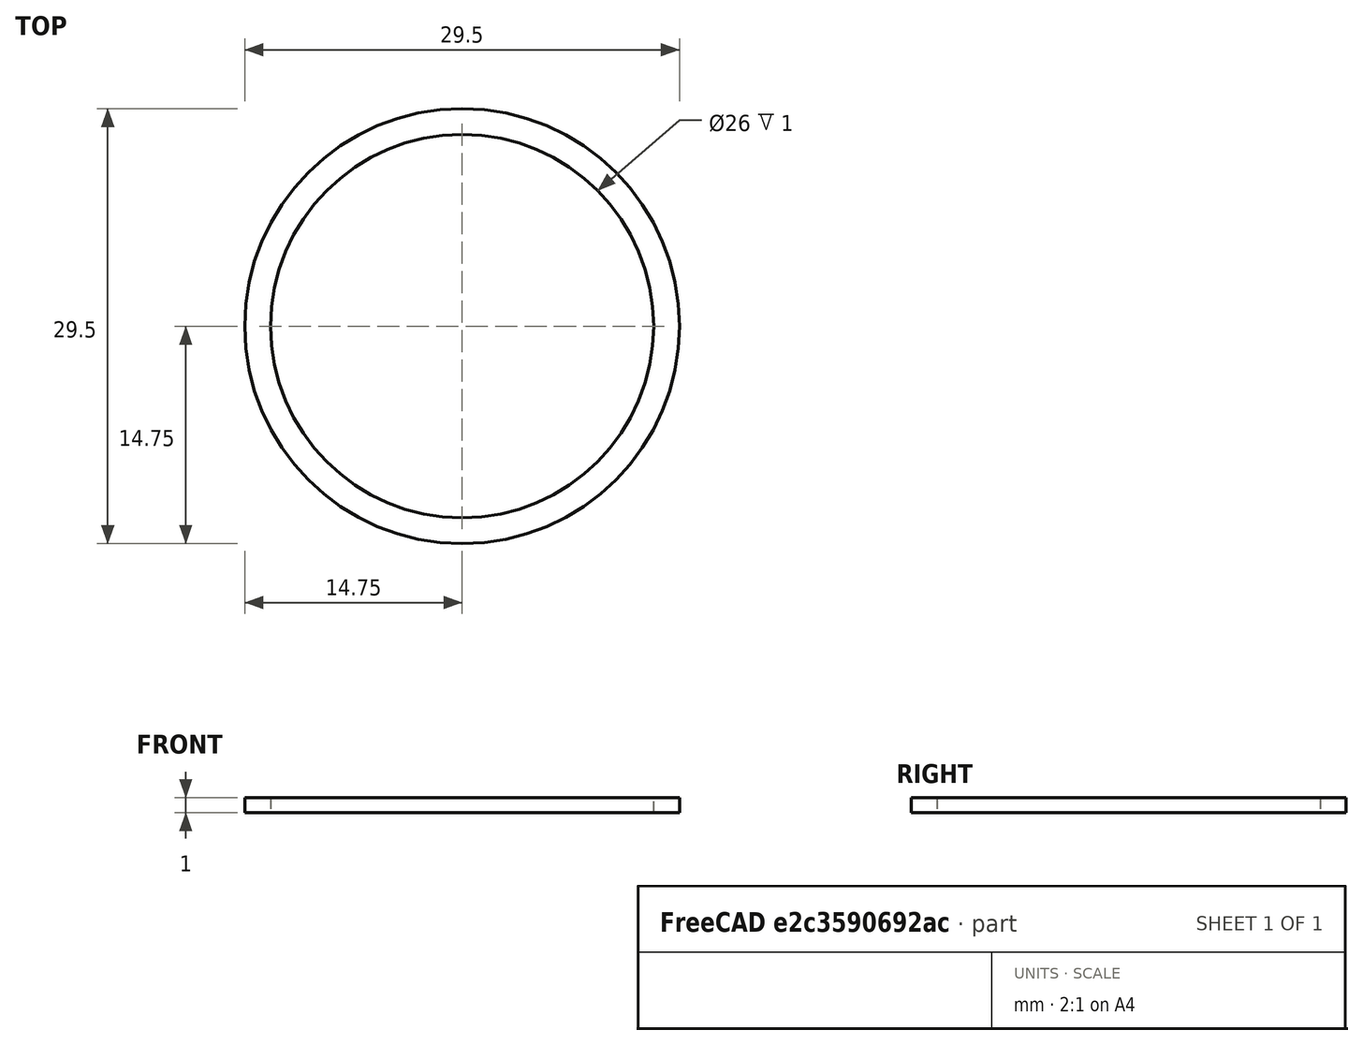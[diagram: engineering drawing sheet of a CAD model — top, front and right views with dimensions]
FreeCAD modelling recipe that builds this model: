
FCSTD DOCUMENT  (FreeCAD 0.19R24276 (Git))
Label: Ring_d26_5__d29_5
License: All rights reserved
LicenseURL: http://en.wikipedia.org/wiki/All_rights_reserved
objects: Sketcher::SketchObject×1, PartDesign::Pad×1, PartDesign::Body×1
note: 4 computed .brp shape members not serialized (recipe doc carries the construction recipe); baked Part::Feature solids carry a one-line shape summary decoded from their .brp

FEATURE [Sketcher::SketchObject] Sketch
  FullyConstrained = true
  MapMode = 5
  Support = -> [XY_Plane]
  sketch-geometry (2):
    g0: Circle CenterX=0 CenterY=0 CenterZ=0 NormalX=0 NormalY=0 NormalZ=1 AngleXU=0 Radius=14.75
    g1: Circle CenterX=0 CenterY=0 CenterZ=0 NormalX=0 NormalY=0 NormalZ=1 AngleXU=0 Radius=13
  constraints (4):
    c: Coincident(g0,g-1)
    c: Diameter(g0) = 29.5
    c: Coincident(g1,g0)
    c: Diameter(g1) = 26
FEATURE [PartDesign::Pad] Pad
  Direction = (1,1,1)
  Length = 1
  Length2 = 100
  Profile = -> Sketch
  Type = 0
FEATURE [PartDesign::Body] Body
  Group = -> [Sketch,Pad]
  Origin = -> Origin
  Tip = -> Pad
